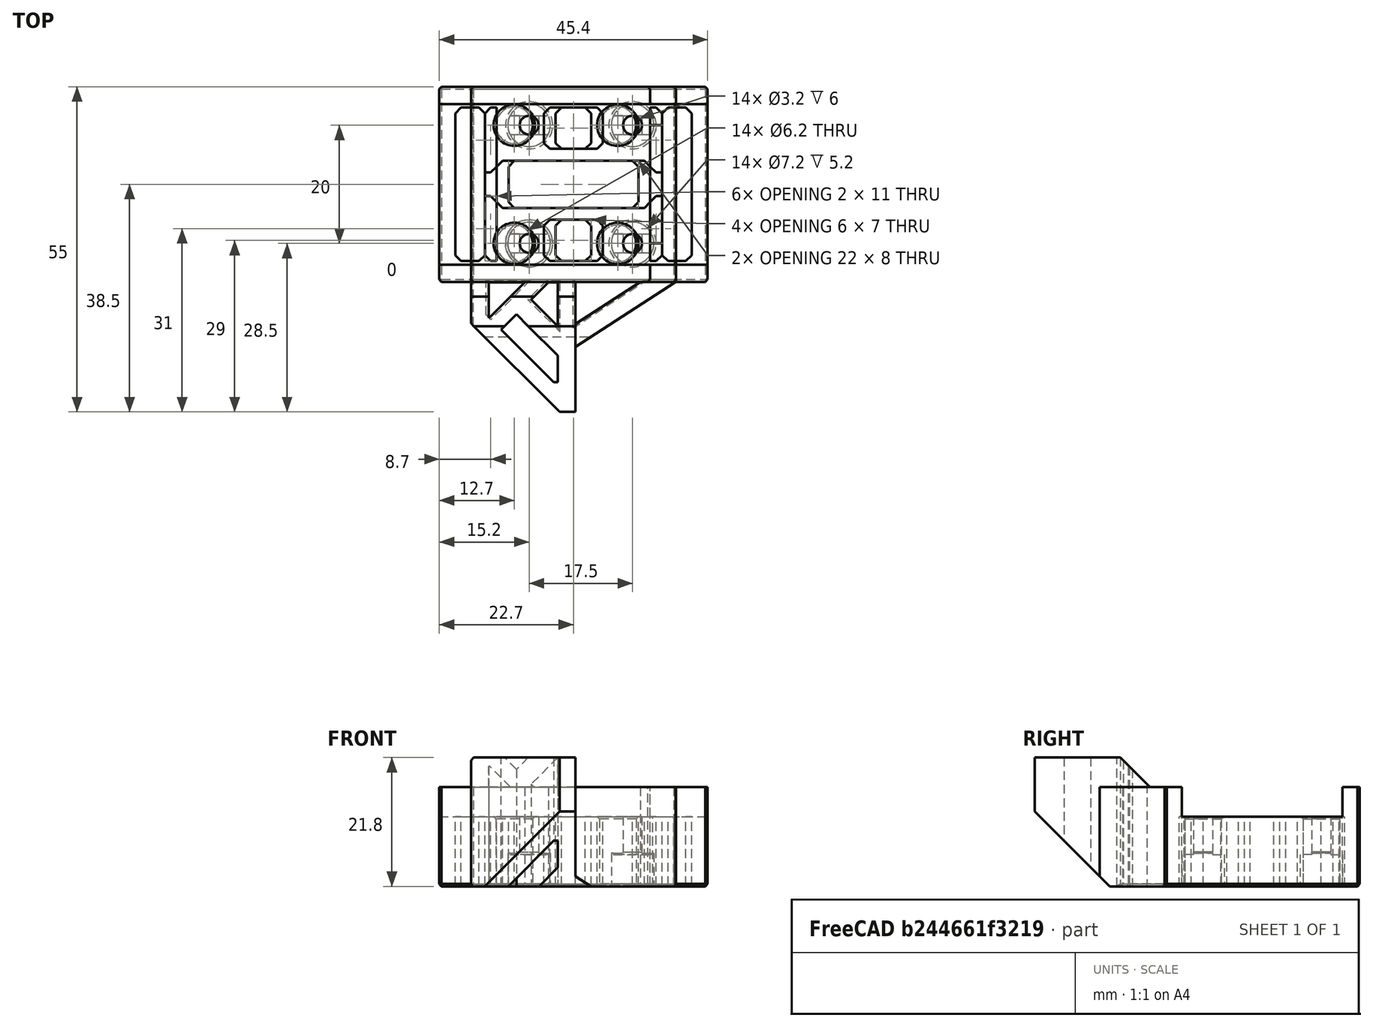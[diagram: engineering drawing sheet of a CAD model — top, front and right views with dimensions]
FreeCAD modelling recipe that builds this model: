
FCSTD DOCUMENT  (FreeCAD 0.18R16146 (Git))
Label: rail-block-mod
License: All rights reserved
LicenseURL: http://en.wikipedia.org/wiki/All_rights_reserved
objects: Part::Box×16, Part::Feature×8, Part::Chamfer×8, Part::MultiFuse×4, Part::Cut×4
note: 40 computed .brp shape members not serialized (recipe doc carries the construction recipe); baked Part::Feature solids carry a one-line shape summary decoded from their .brp

FEATURE [Part::Feature] Fusion004009005002004005004001  label="fds"
  Placement = pos=(-22.7,1e-15,11.8) rot=(1,0,0;3.14159rad)
  shape: bbox 45.4 x 33 x 16.8 mm, 40 faces (baked)
FEATURE [Part::Feature] Chamfer005013001  label="12CA-1180"
  Placement = pos=(-17.35,2e-15,11.8) rot=(1,0,0;3.14159rad)
  shape: bbox 34.7 x 55 x 21.8 mm, 75 faces (baked)
FEATURE [Part::Chamfer] Chamfer  label="12H-solid"
  Base = -> Fusion004009005002004005004001
  Edges = 14 edges r=0.4: [Edge23,Edge35,Edge36,Edge37,Edge38,Edge39,Edge40,Edge41,Edge56,Edge58,Edge101,Edge102,Edge103,Edge104]
FEATURE [Part::Chamfer] Chamfer005013002  label="12CA-solid"
  Base = -> Chamfer005013001
  Edges = 12 edges r=0.4: [Edge40,Edge41,Edge42,Edge43,Edge44,Edge45,Edge46,Edge47,Edge48,Edge50,Edge169,Edge171]
FEATURE [Part::Feature] Chamfer005013003001  label="12C-solid001"
  shape: bbox 34.7 x 33 x 16.8 mm, 58 faces (baked)
FEATURE [Part::Feature] Chamfer005013003002  label="12H-solid001"
  shape: bbox 45.4 x 33 x 16.8 mm, 58 faces (baked)
FEATURE [Part::Feature] Chamfer005013002001  label="12CA-solid001"
  shape: bbox 34.7 x 55 x 21.8 mm, 87 faces (baked)
FEATURE [Part::Box] Box  label="Cube"
  AttacherType = Attacher::AttachEngine3D
  Height = 13
  Length = 26
  Placement = pos=(-13,-4,0) rot=(0,0,1;0rad)
  Width = 8
FEATURE [Part::Box] Box001  label="Cube001"
  AttacherType = Attacher::AttachEngine3D
  Height = 13
  Length = 10
  Placement = pos=(-5,6,0) rot=(0,0,1;0rad)
  Width = 7
FEATURE [Part::Box] Box002  label="Cube002"
  AttacherType = Attacher::AttachEngine3D
  Height = 13
  Length = 10
  Placement = pos=(-5,-13,0) rot=(0,0,1;0rad)
  Width = 7
FEATURE [Part::Box] Box004  label="Cube004"
  AttacherType = Attacher::AttachEngine3D
  Height = 13
  Length = 5
  Placement = pos=(-20,-13,0) rot=(0,0,1;0rad)
  Width = 26
FEATURE [Part::Box] Box007  label="Cube007"
  AttacherType = Attacher::AttachEngine3D
  Height = 13
  Length = 22
  Placement = pos=(-11,-4,0) rot=(0,0,1;0rad)
  Width = 8
FEATURE [Part::Box] Box008  label="Cube008"
  AttacherType = Attacher::AttachEngine3D
  Height = 13
  Length = 2
  Placement = pos=(-15,2,0) rot=(0,0,1;0rad)
  Width = 11
FEATURE [Part::Box] Box009  label="Cube009"
  AttacherType = Attacher::AttachEngine3D
  Height = 13
  Length = 6
  Placement = pos=(-3,6,0) rot=(0,0,1;0rad)
  Width = 7
FEATURE [Part::Box] Box010  label="Cube010"
  AttacherType = Attacher::AttachEngine3D
  Height = 13
  Length = 6
  Placement = pos=(-3,-13,0) rot=(0,0,1;0rad)
  Width = 7
FEATURE [Part::Box] Box011  label="Cube011"
  AttacherType = Attacher::AttachEngine3D
  Height = 13
  Length = 2
  Placement = pos=(-15,-13,0) rot=(0,0,1;0rad)
  Width = 11
FEATURE [Part::Box] Box012  label="Cube012"
  AttacherType = Attacher::AttachEngine3D
  Height = 13
  Length = 2
  Placement = pos=(13,2,0) rot=(0,0,1;0rad)
  Width = 11
FEATURE [Part::Box] Box013  label="Cube013"
  AttacherType = Attacher::AttachEngine3D
  Height = 13
  Length = 2
  Placement = pos=(13,-13,0) rot=(0,0,1;0rad)
  Width = 11
FEATURE [Part::MultiFuse] Fusion  label="12c-cut"
  Placement = pos=(0,0,0.2) rot=(0,0,1;0rad)
  Shapes = -> [Box007,Box008,Box011,Box012,Box009,Box013,Box010]
FEATURE [Part::Feature] Fusion004009005002004005004002  label="12c-cut001"
  Placement = pos=(0,0,0.2) rot=(0,0,1;0rad)
  shape: bbox 30 x 26 x 13 mm, 42 faces, 7 solids (baked)
FEATURE [Part::Box] Box014  label="Cube014"
  AttacherType = Attacher::AttachEngine3D
  Height = 13
  Length = 5
  Placement = pos=(15,-13,0) rot=(0,0,1;0rad)
  Width = 26
FEATURE [Part::MultiFuse] Fusion004009005002004005004003
  Placement = pos=(0,0,0.2) rot=(0,0,1;0rad)
  Shapes = -> [Box004,Box,Box002,Box001,Box014]
FEATURE [Part::Cut] Cut
  Base = -> Chamfer005013003001
  Tool = -> Fusion
FEATURE [Part::Chamfer] Chamfer005013003009  label="12c-hollow"
  Base = -> Cut
  Edges = 19 edges r=1: [Edge66,Edge71,Edge75,Edge77,Edge87,Edge88,Edge90,Edge92,Edge95,Edge96,Edge100,Edge110,Edge111,Edge113,Edge115,Edge119,Edge121,Edge126,Edge131]
FEATURE [Part::Cut] Cut003
  Base = -> Chamfer005013002001
  Tool = -> Fusion004009005002004005004002
FEATURE [Part::Chamfer] Chamfer005013003010  label="12ca-hollow"
  Base = -> Cut003
  Edges = 20 edges r=1: [Edge251,Edge256,Edge260,Edge262,Edge272,Edge273,Edge275,Edge277,Edge280,Edge281,Edge283,Edge285,Edge293,Edge294,Edge296,Edge298,Edge302,Edge304,Edge309,Edge314]
FEATURE [Part::Cut] Cut004
  Base = -> Chamfer005013003002
  Tool = -> Fusion004009005002004005004003
FEATURE [Part::Chamfer] Chamfer005013003011  label="12h-hollow"
  Base = -> Cut004
  Edges = 20 edges r=1: [Edge157,Edge158,Edge160,Edge162,Edge165,Edge166,Edge168,Edge170,Edge173,Edge174,Edge176,Edge178,Edge181,Edge182,Edge184,Edge186,Edge189,Edge190,Edge192,Edge194]
FEATURE [Part::Box] Box015  label="Cube015"
  AttacherType = Attacher::AttachEngine3D
  Height = 21
  Length = 20
  Placement = pos=(-33,-23.6,0) rot=(0,0,1;0rad)
  Width = 10
FEATURE [Part::Box] Box016  label="Cube016"
  AttacherType = Attacher::AttachEngine3D
  Height = 21
  Length = 20
  Placement = pos=(-33,13.6,0) rot=(0,0,1;0rad)
  Width = 10
FEATURE [Part::Feature] Chamfer005013003009001  label="12c-hollow001"
  shape: bbox 34.7 x 33 x 16.8 mm, 112 faces (baked)
FEATURE [Part::MultiFuse] Fusion004009005002004005004004
  Placement = pos=(46,0,0) rot=(0,0,1;0rad)
  Shapes = -> [Box016,Box015]
FEATURE [Part::Chamfer] Chamfer005013003009005  label="12-c-mod"
  Base = -> Chamfer005013003009001
  Edges = 1 edges r=1: [Edge135]
FEATURE [Part::Cut] Cut005
  Base = -> Chamfer005013003009
  Tool = -> Fusion004009005002004005004004
FEATURE [Part::Chamfer] Chamfer005013003009006
  Base = -> Cut005
  Edges = 1 edges r=1: [Edge141]
FEATURE [Part::Box] Box017  label="Cube017"
  AttacherType = Attacher::AttachEngine3D
  Height = 11.8
  Length = 4
  Placement = pos=(12,-13,0) rot=(0,0,1;0rad)
  Width = 3
FEATURE [Part::Box] Box018  label="Cube018"
  AttacherType = Attacher::AttachEngine3D
  Height = 11.8
  Length = 4
  Placement = pos=(12,10,0) rot=(0,0,1;0rad)
  Width = 3
FEATURE [Part::MultiFuse] Fusion004009005002004005004005
  Shapes = -> [Chamfer005013003009006,Box017,Box018]
FEATURE [Part::Chamfer] Chamfer005013003009007
  Base = -> Fusion004009005002004005004005
  Edges = 6 edges r=0.4: [Edge89,Edge90,Edge93,Edge94,Edge216,Edge218]
FEATURE [Part::Feature] Chamfer005013003009007001  label="12c-trim"
  shape: bbox 34.7 x 33 x 16.8 mm, 117 faces (baked)
